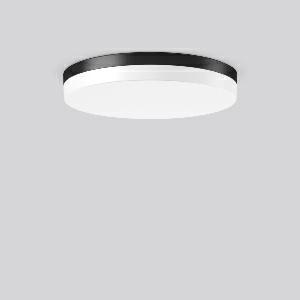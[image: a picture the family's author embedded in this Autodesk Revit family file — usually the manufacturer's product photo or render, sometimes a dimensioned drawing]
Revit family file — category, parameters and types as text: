
# Revit family: flat_slim_round_312633_0031_19_517f
name_source: partatom
category: Lighting Fixtures
units: mm (PartAtom-declared; Revit-internal decimal feet)

## family parameters
Cut with Voids When Loaded = No
Host = Face
Light Source = No
Part Type = Normal
Room Calculation Point = No
Round Connector Dimension = Use Diameter
Shared = No

## types (1)
- MultiLumen 1 830 (1 x LED Modul 830, 3350 lm, 3000)
    Apparent Load = 31 VA
    CIE Flux Codes = 41 71 90 86 100
    Color Rendering = 80
    Color Temperature = 3000
    Default Elevation = 1800 mm
    Height = 75 mm
    Lamp = 1 x LED Modul 830
    Lamp Light Flux = 3350 lm
    Lamp count = 1
    Length = 480 mm
    Lifetime = 50000 h
    Luminous efficacy = 108 lm/W
    Manufacturer = RZB
    ModVariant = No
    Model = 312633.0031.19
    Mounting Place = Ceiling
    Mounting Type = Surface mounted
    Number of Poles = 1
    OnlyDefault = Yes
    Power Factor = 1
    Product Name = FLAT SLIM round
    Product group = Surface mounted ceiling and wall luminaires
    ProductGroupID = 305
    Protection Class = Protection class I
    Protection Degree = Degree of protection
    RLX_Detail_Level = 1
    RLX_Emergency_Light_Flux = 0 lm
    RLX_Emergency_Type = 0
    RLX_Emergency_Type_DB = No
    RlxData = <blob elided: 23313 chars, md5=bc6ebe78>
    Socket = socket
    Standby Power = 0 W
    System Light Flux = 3350 lm
    System Power = 31 W
    Type Comments = MultiLumen 1 830
    Type Image = 312633.0031.jpg
    URL = http://relux.com
    VarID = multilumen_1_830
    Voltage = 0 V
    Weight = 0.00 kg
    Width = 0 mm  [stored 0 ft]

note: [stored X ft] marks values corroborated as IEEE doubles in the binary element streams (Revit-internal decimal feet)

## geometry (parser evidence)
native form markers: Blend x4, Sweep x13
no freeform markers — native parametric forms only
